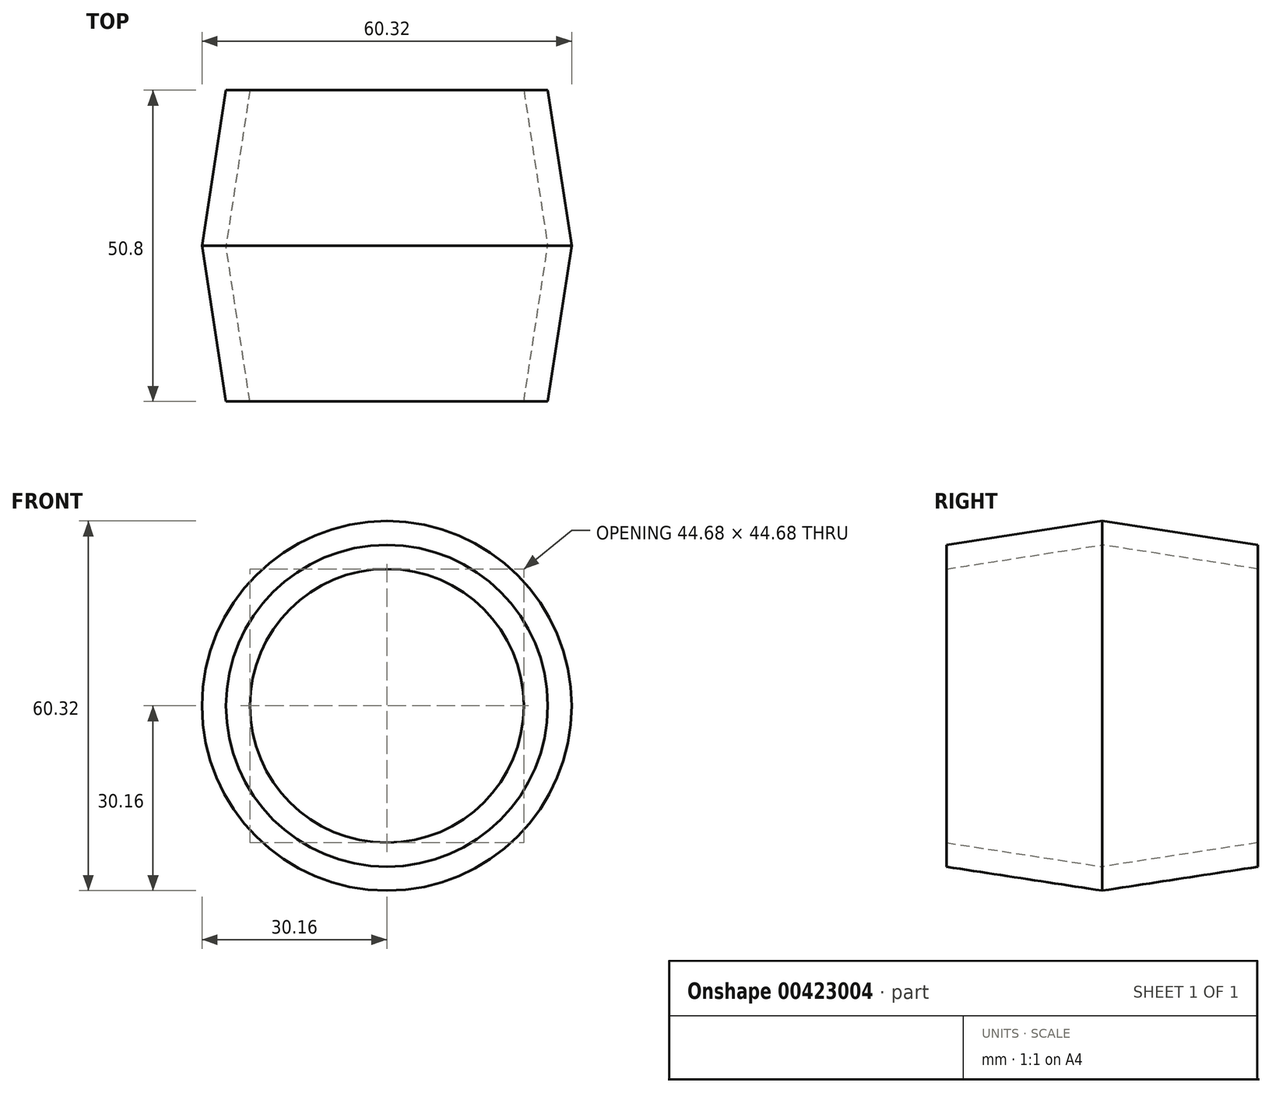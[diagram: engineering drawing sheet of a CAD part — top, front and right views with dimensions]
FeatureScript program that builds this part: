
annotation { "Feature Type Name" : "Feature", "Feature Type Description" : "" }
export const myFeature = defineFeature(function(context is Context, id is Id, definition is map)
    precondition{}
    {
        {
            var Q0;
            Q0=qCreatedBy(makeId("Front.planeOp"),FACE);
            var sketch = newSketch(context, id + "F0", { "sketchPlane" : qUnion([Q0])});
            skCircle(sketch, "E0", {"center": v(0, 0) * mm, "radius": 30.16 * mm});
            skLineSegment(sketch, "E1", {"start": v(0, 0) * mm, "end": v(0, 30.16) * mm, "construction": true});
            skSolve(sketch);
        }
        {
            var Q0;
            Q0=qCreatedBy(makeId("Front.planeOp"),FACE);
            cPlane(context, id + "F1", {"entities" : qUnion([Q0]), "cplaneType" : CPlaneType.OFFSET, "offset" : 25.4 * mm, "width" : 152.4 * mm, "height" : 152.4 * mm});
        }
        {
            var Q0;
            Q0=qCreatedBy(id+"F1.planeOp",FACE);
            var sketch = newSketch(context, id + "F2", { "sketchPlane" : qUnion([Q0])});
            skCircle(sketch, "E2", {"center": v(0, 0) * mm, "radius": 26.25 * mm});
            skLineSegment(sketch, "E3", {"start": v(0, 0) * mm, "end": v(0, 26.25) * mm, "construction": true});
            skSolve(sketch);
        }
        {
            var Q0;
            Q0=makeQuery(id+"F2.imprint","IMPRINT",FACE,{"disambiguationData":[TD([[makeQuery(id+"F2.imprint","IMPRINT",EDGE,{"derivedFrom":sQuery(id+"F2.wireOp",EDGE,"E2")}),1.0]])]});
            var Q1;
            Q1=makeQuery(id+"F0.imprint","IMPRINT",FACE,{"disambiguationData":[TD([[makeQuery(id+"F0.imprint","IMPRINT",EDGE,{"derivedFrom":sQuery(id+"F0.wireOp",EDGE,"E0")}),1.0]])]});
            loft(context, id + "F3", {"sheetProfilesArray" : [{ "sheetProfileEntities" : qUnion([Q0]) }, { "sheetProfileEntities" : qUnion([Q1]) }]});
        }
        {
            var Q0;
            Q0=makeQuery(id+"F3.opLoft","CAP_FACE",FACE,{"disambiguationData":[OSD([makeQuery(id+"F2.imprint","IMPRINT",FACE,{"disambiguationData":[TD([[makeQuery(id+"F2.imprint","IMPRINT",EDGE,{"derivedFrom":sQuery(id+"F2.wireOp",EDGE,"E2")}),1.0]])]})])],"isStart":true});
            var sketch = newSketch(context, id + "F4", { "sketchPlane" : qUnion([Q0])});
            skCircle(sketch, "E4", {"center": v(0, 0) * mm, "radius": 22.34 * mm});
            skSolve(sketch);
        }
        {
            var Q0;
            Q0=makeQuery(id+"F3.opLoft","CAP_FACE",FACE,{"disambiguationData":[OSD([makeQuery(id+"F0.imprint","IMPRINT",FACE,{"disambiguationData":[TD([[makeQuery(id+"F0.imprint","IMPRINT",EDGE,{"derivedFrom":sQuery(id+"F0.wireOp",EDGE,"E0")}),1.0]])]})])],"isStart":true});
            var sketch = newSketch(context, id + "F5", { "sketchPlane" : qUnion([Q0])});
            skCircle(sketch, "E5", {"center": v(0, 0) * mm, "radius": 26.25 * mm});
            skSolve(sketch);
        }
        {
            var Q1;
            Q1=makeQuery(id+"F5.imprint","IMPRINT",FACE,{"disambiguationData":[TD([[makeQuery(id+"F5.imprint","IMPRINT",EDGE,{"derivedFrom":sQuery(id+"F5.wireOp",EDGE,"E5")}),1.0]])]});
            var Q2;
            Q2=makeQuery(id+"F4.imprint","IMPRINT",FACE,{"disambiguationData":[TD([[makeQuery(id+"F4.imprint","IMPRINT",EDGE,{"derivedFrom":sQuery(id+"F4.wireOp",EDGE,"E4")}),1.0]])]});
            loft(context, id + "F6", {"operationType" : NewBodyOperationType.REMOVE, "sheetProfilesArray" : [{ "sheetProfileEntities" : qUnion([Q1]) }, { "sheetProfileEntities" : qUnion([Q2]) }]});
        }
        {
            var Q0;
            Q0=makeQuery(id+"F3.opLoft","SWEPT_BODY",BODY,{"disambiguationData":[OSD([makeQuery(id+"F0.imprint","IMPRINT",FACE,{"disambiguationData":[TD([[makeQuery(id+"F0.imprint","IMPRINT",EDGE,{"derivedFrom":sQuery(id+"F0.wireOp",EDGE,"E0")}),1.0]])]}),makeQuery(id+"F2.imprint","IMPRINT",FACE,{"disambiguationData":[TD([[makeQuery(id+"F2.imprint","IMPRINT",EDGE,{"derivedFrom":sQuery(id+"F2.wireOp",EDGE,"E2")}),1.0]])]})])]});
            var Q1;
            Q1=makeQuery(id+"F3.opLoft","CAP_FACE",FACE,{"disambiguationData":[OSD([makeQuery(id+"F0.imprint","IMPRINT",FACE,{"disambiguationData":[TD([[makeQuery(id+"F0.imprint","IMPRINT",EDGE,{"derivedFrom":sQuery(id+"F0.wireOp",EDGE,"E0")}),1.0]])]})])],"isStart":true});
            mirror(context, id + "F7", {"operationType" : NewBodyOperationType.ADD, "entities" : qUnion([Q0]), "mirrorPlane" : qUnion([Q1])});
        }
    });
